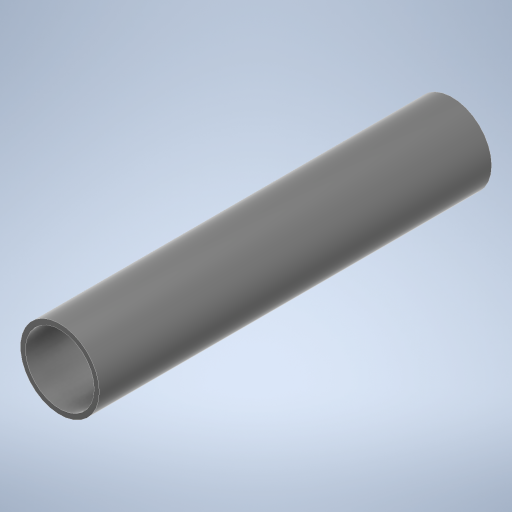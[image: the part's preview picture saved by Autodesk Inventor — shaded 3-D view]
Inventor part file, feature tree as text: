
AUTODESK INVENTOR PART (.ipt)
format: ipt  version: 2024 (Build 280153000, 153)  size: 236,544 bytes
history: native  units: mm
features: extrude x1
ambient origin geometry x8: Origin, YZ Plane, XZ Plane, XY Plane, X Axis, Y Axis, Z Axis, Center Point
bodies: Solid1 (feature_tree)
feature tree (1):
  extrude  "Extrusion1"  Depth=60.325mm
